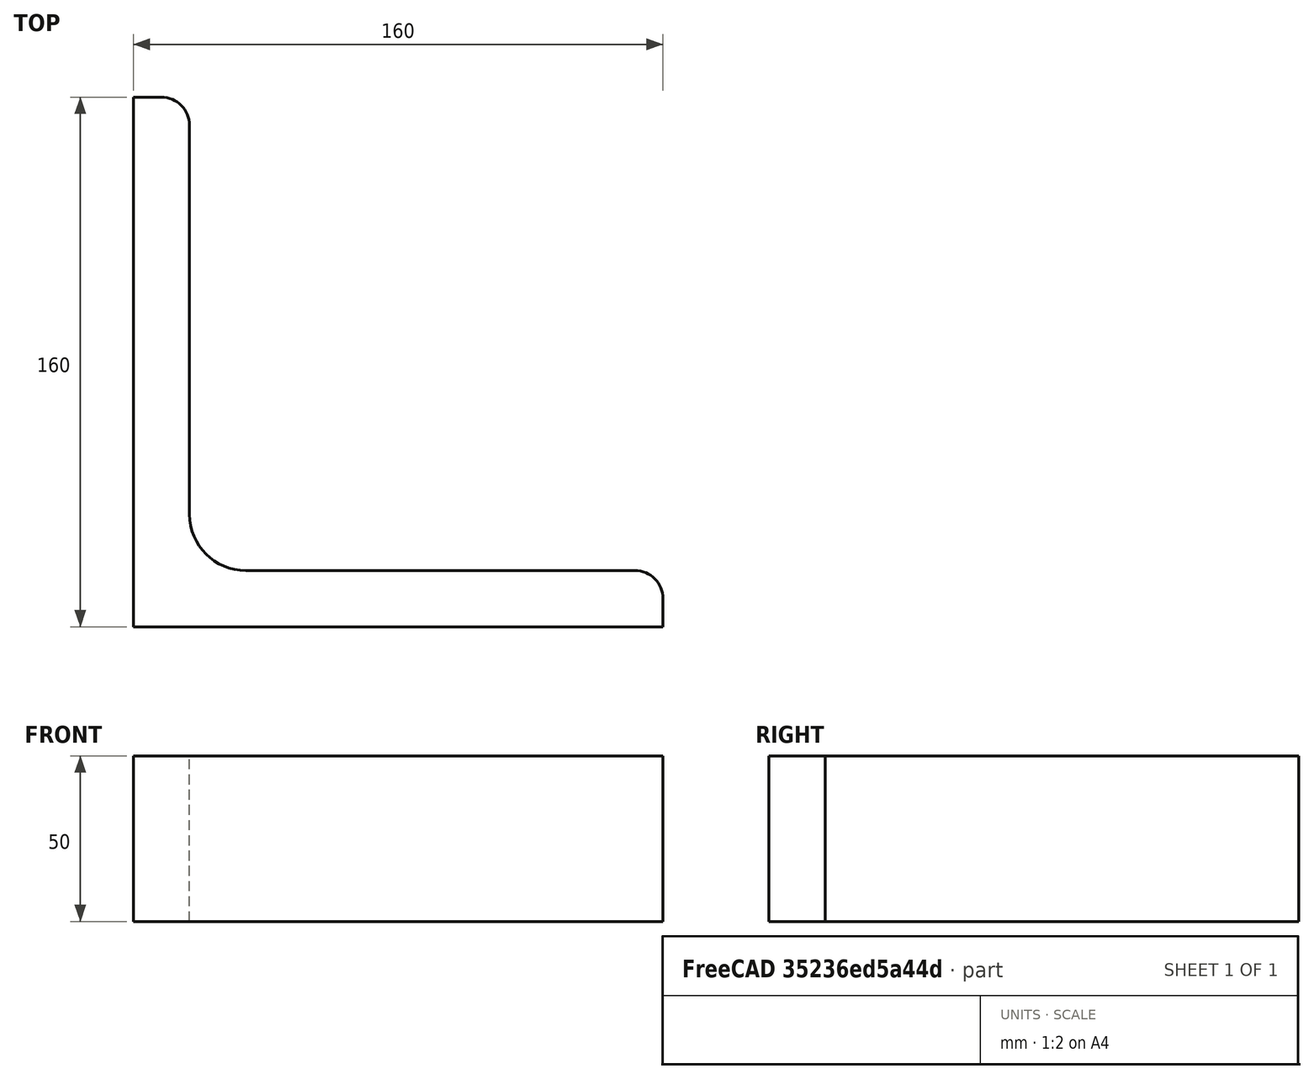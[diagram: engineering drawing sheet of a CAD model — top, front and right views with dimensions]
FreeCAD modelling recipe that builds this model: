
FCSTD DOCUMENT  (FreeCAD 0.15R4671 (Git))
Label: Angle Bar L160x160x17 EN10056 S235JR
License: All rights reserved
LicenseURL: http://en.wikipedia.org/wiki/All_rights_reserved
objects: Sketcher::SketchObject×1, Part::Extrusion×1
note: 2 computed .brp shape members not serialized (recipe doc carries the construction recipe); baked Part::Feature solids carry a one-line shape summary decoded from their .brp

FEATURE [Sketcher::SketchObject] Sketch
  sketch-geometry (9):
    g0: LineSegment StartX=0 StartY=0 StartZ=0 EndX=160 EndY=0 EndZ=0
    g1: LineSegment StartX=160 StartY=0 StartZ=0 EndX=160 EndY=8.5 EndZ=0
    g2: LineSegment StartX=151.5 StartY=17 StartZ=0 EndX=34 EndY=17 EndZ=0
    g3: LineSegment StartX=0 StartY=0 StartZ=0 EndX=0 EndY=160 EndZ=0
    g4: LineSegment StartX=0 StartY=160 StartZ=0 EndX=8.5 EndY=160 EndZ=0
    g5: LineSegment StartX=17 StartY=151.5 StartZ=0 EndX=17 EndY=34 EndZ=0
    g6: ArcOfCircle CenterX=34 CenterY=34 CenterZ=0 NormalX=0 NormalY=0 NormalZ=1 Radius=17 StartAngle=3.14159 EndAngle=4.71239
    g7: ArcOfCircle CenterX=8.5 CenterY=151.5 CenterZ=0 NormalX=0 NormalY=0 NormalZ=1 Radius=8.5 StartAngle=0 EndAngle=1.5708
    g8: ArcOfCircle CenterX=151.5 CenterY=8.5 CenterZ=0 NormalX=0 NormalY=0 NormalZ=1 Radius=8.5 StartAngle=0 EndAngle=1.5708
  constraints (23):
    c: Coincident(g0,g-1)
    c: Horizontal(g0)
    c: Coincident(g1,g0)
    c: Vertical(g1)
    c: Horizontal(g2)
    c: Coincident(g3,g-1)
    c: Vertical(g3)
    c: Coincident(g4,g3)
    c: Horizontal(g4)
    c: Vertical(g5)
    c: Tangent(g5,g6) = -1.5708
    c: Tangent(g2,g6) = 1.5708
    c: Tangent(g4,g7) = 1.5708
    c: Tangent(g5,g7) = 1.5708
    c: Tangent(g2,g8) = -1.5708
    c: Tangent(g1,g8) = -1.5708
    c: DistanceX(g0) = 160
    c: DistanceY(g3) = 160
    c: DistanceY(g0,g2) = 17
    c: DistanceX(g3,g5) = 17
    c: Radius(g6) = 17
    c: Radius(g8) = 8.5
    c: Radius(g7) = 8.5
FEATURE [Part::Extrusion] Extrude  label="Angle Bar L160x160x17 EN10056 S235JR"
  Base = -> Sketch
  Dir = (0,0,50)
  Solid = true
